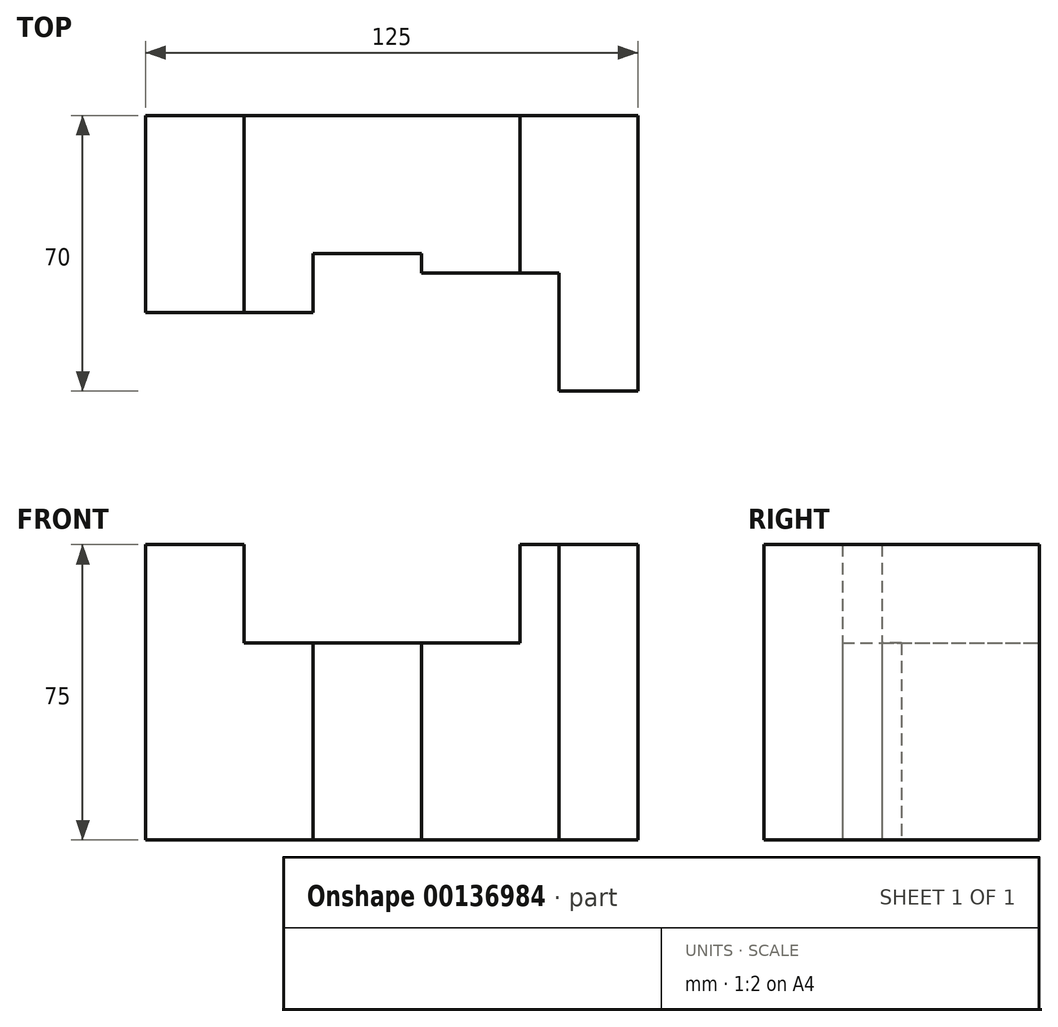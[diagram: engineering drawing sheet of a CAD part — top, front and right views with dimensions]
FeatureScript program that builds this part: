
annotation { "Feature Type Name" : "Feature", "Feature Type Description" : "" }
export const myFeature = defineFeature(function(context is Context, id is Id, definition is map)
    precondition{}
    {
        {
            var Q0;
            Q0=qCreatedBy(makeId("Front.planeOp"),FACE);
            var sketch = newSketch(context, id + "F0", { "sketchPlane" : qUnion([Q0])});
            skLineSegment(sketch, "E0", {"start": v(-62.5, 0) * mm, "end": v(-62.5, 75) * mm});
            skLineSegment(sketch, "E1", {"start": v(-62.5, 75) * mm, "end": v(-37.5, 75) * mm});
            skLineSegment(sketch, "E2", {"start": v(-37.5, 75) * mm, "end": v(-37.5, 50) * mm});
            skLineSegment(sketch, "E3", {"start": v(-37.5, 50) * mm, "end": v(32.5, 50) * mm});
            skLineSegment(sketch, "E4", {"start": v(32.5, 50) * mm, "end": v(32.5, 75) * mm});
            skLineSegment(sketch, "E5", {"start": v(32.5, 75) * mm, "end": v(62.5, 75) * mm});
            skLineSegment(sketch, "E6", {"start": v(62.5, 75) * mm, "end": v(62.5, 0) * mm});
            skLineSegment(sketch, "E7", {"start": v(62.5, 0) * mm, "end": v(-62.5, 0) * mm});
            skLineSegment(sketch, "E8", {"start": v(-20, 50) * mm, "end": v(-20, 0) * mm});
            skLineSegment(sketch, "E9", {"start": v(7.5, 50) * mm, "end": v(7.5, 0) * mm});
            skLineSegment(sketch, "E10", {"start": v(42.5, 75) * mm, "end": v(42.5, 0) * mm});
            skSolve(sketch);
        }
        {
            var Q0;
            Q0 = qSketchRegion(id + "F0", true);
            extrude(context, id + "F1", {"entities" : qUnion([Q0]), "endBound" : BoundingType.SYMMETRIC, "depth" : 70 * mm});
        }
        {
            var Q0;
            Q0=qCreatedBy(makeId("Top.planeOp"),FACE);
            var sketch = newSketch(context, id + "F2", { "sketchPlane" : qUnion([Q0])});
            skLineSegment(sketch, "E11.bottom", {"start": v(-62.5, -35) * mm, "end": v(42.5, -35) * mm});
            skLineSegment(sketch, "E11.top", {"start": v(7.5, -5) * mm, "end": v(42.5, -5) * mm});
            skLineSegment(sketch, "E11.left", {"start": v(-62.5, -35) * mm, "end": v(-62.5, -15) * mm});
            skLineSegment(sketch, "E11.right", {"start": v(42.5, -35) * mm, "end": v(42.5, -5) * mm});
            skLineSegment(sketch, "E12.top", {"start": v(-20, 0) * mm, "end": v(7.5, 0) * mm});
            skLineSegment(sketch, "E12.right", {"start": v(7.5, -5) * mm, "end": v(7.5, 0) * mm});
            skLineSegment(sketch, "E13.top", {"start": v(-20, -15) * mm, "end": v(-62.5, -15) * mm});
            skLineSegment(sketch, "E14", {"start": v(-20, 0) * mm, "end": v(-20, -15) * mm});
            skSolve(sketch);
        }
        {
            var Q0;
            Q0 = qSketchRegion(id + "F2", true);
            extrude(context, id + "F3", {"entities" : qUnion([Q0]), "operationType" : NewBodyOperationType.REMOVE, "depth" : 75 * mm});
        }
    });
